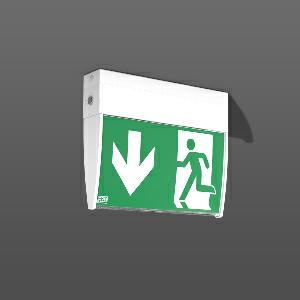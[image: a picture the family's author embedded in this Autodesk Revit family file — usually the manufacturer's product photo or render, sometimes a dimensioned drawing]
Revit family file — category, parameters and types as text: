
# Revit family: gsun_d_671996_002_2_89_1ce3
name_source: partatom
category: Lighting Fixtures
units: mm (PartAtom-declared; Revit-internal decimal feet)

## family parameters
Cut with Voids When Loaded = No
Host = Face
Light Source = No
Part Type = Normal
Room Calculation Point = No
Round Connector Dimension = Use Diameter
Shared = No

## types (1)
- GSUN D
    Apparent Load = 0 VA
    Default Elevation = 1800 mm
    Description = Series: GSUN D
Luminaire for escape route identification. Housing: extruded aluminium profile, powder-coated. 4 legends and 1 white lay in plastic sheet included. Universal mounting kit for ceiling and wall surface mounting. Driver integrated. Suitable for connection to central battery systems. With AC Control monitoring module for LUXIFAIR central battery units. 
Colour: white
Length: 247 mm
Width: 45 mm
Height: 200 mm
Weight: 1 kg
Operating mode: maintained power mode
Viewing Distance: 24 m
Lamp: LED
Socket: without socket
Colour temperature: 4000K
System power: 4.7 W
System power, emergency: 4.7 W
Control gear: Converter not necessary
Protection class: I
Type of protection: IP 30
    Height = 200 mm  [stored 0.656168 ft]
    Lamp = 0 x
    Length = 247 mm
    Luminous efficacy = 0 lm/W
    Manufacturer = RZB
    ModVariant = No
    Model = 671996.002.2.89
    Mounting Place = Ceiling, Wall
    Mounting Type = Surface mounted
    Number of Poles = 1
    OnlyDefault = Yes
    Power Factor = 1
    Product Name = GSUN D
    Product group = Surface mounted ceiling and wall luminaires
    ProductGroupID = 305
    Protection Class = Protection class I
    Protection Degree = IP 30
    RLX_Detail_Level = 1
    RLX_Emergency_Light_Flux = 0 lm
    RLX_Emergency_Type = 0
    RLX_Emergency_Type_DB = No
    RlxData = <blob elided: 29977 chars, md5=27880089>
    Standby Power = 0 W
    System Light Flux = 0 lm
    System Power = 0 W
    Type Comments = Product without accessories
    Type Image = 671995.002.1.jpg
    URL = http://relux.com
    VarID = ---
    Voltage = 230 V
    Voltage Range = 220-240 V
    Weight = 0.00 kg
    Width = 45 mm

note: [stored X ft] marks values corroborated as IEEE doubles in the binary element streams (Revit-internal decimal feet)

## geometry (parser evidence)
native form markers: Blend x4, Sweep x10
no freeform markers — native parametric forms only
